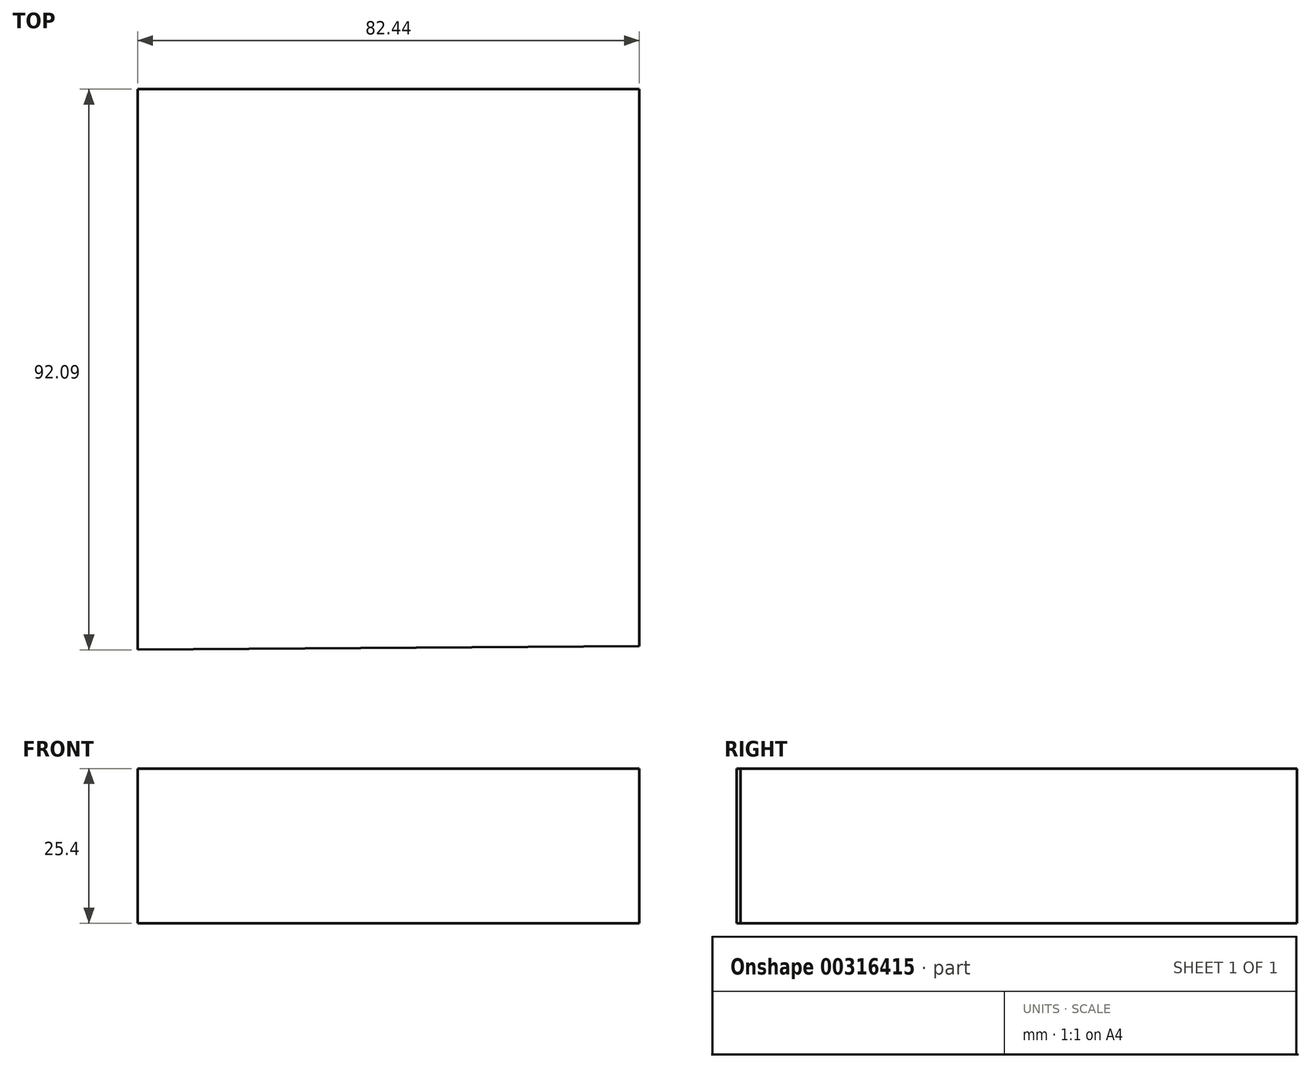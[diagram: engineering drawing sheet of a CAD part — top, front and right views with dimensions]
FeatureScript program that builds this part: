
annotation { "Feature Type Name" : "Feature", "Feature Type Description" : "" }
export const myFeature = defineFeature(function(context is Context, id is Id, definition is map)
    precondition{}
    {
        {
            var Q0;
            Q0=qCreatedBy(makeId("Top.planeOp"),FACE);
            var sketch = newSketch(context, id + "F0", { "sketchPlane" : qUnion([Q0])});
            skLineSegment(sketch, "E0", {"start": v(-44.36, -45.13) * mm, "end": v(-44.36, 46.96) * mm});
            skLineSegment(sketch, "E1", {"start": v(-44.36, 46.96) * mm, "end": v(38.08, 46.96) * mm});
            skLineSegment(sketch, "E2", {"start": v(38.08, 46.96) * mm, "end": v(38.08, -44.5) * mm});
            skLineSegment(sketch, "E3", {"start": v(38.08, -44.5) * mm, "end": v(-44.36, -45.13) * mm});
            skSolve(sketch);
        }
        {
            var Q0;
            Q0 = qSketchRegion(id + "F0", true);
            extrude(context, id + "F1", {"entities" : qUnion([Q0]), "depth" : 25.4 * mm});
        }
    });
